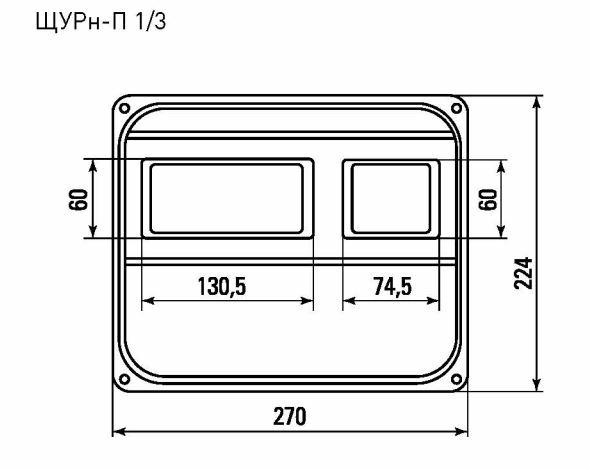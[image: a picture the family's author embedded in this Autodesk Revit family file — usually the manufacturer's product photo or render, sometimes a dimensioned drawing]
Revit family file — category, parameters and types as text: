
# Revit family: EKF_EE_ЩУРв_IP31_PROxima
name_source: partatom
category: Электрооборудование
units: mm (PartAtom-declared; Revit-internal decimal feet)

## family parameters
Всегда вертикально = Да
На основе рабочей плоскости = Нет
Общий = Нет
При загрузке вырезать с полостями = Нет
Размер круглого соединителя = Использовать диаметр
Тип детали = Силовой щит
Точка расчета площади = Да

## types (7) — shared parameters
ADSK_Единица измерения = компл.
ADSK_Завод-изготовитель = EKF
ADSK_Классификация нагрузок = Прочее
ADSK_Количество = 1
ADSK_Коэффициент мощности = 1
ADSK_Напряжение = 400 В
ADSK_Номинальная мощность = 0 Вт
ADSK_Полная мощность = 0 В·А
ADSK_Ток = 125 А
Изготовитель = EKF
Серия номенклатуры = PROxima
Степень защиты IP = IP31
ТВ = EKF
Тип установки = Встраиваемый
zero-valued in all types: ADSK_Масса, Количество DIN-реек

## per-type parameters (varying)
| type | ADSK_Код изделия | ADSK_Количество фаз | ADSK_Марка | ADSK_Материал | ADSK_Наименование | ADSK_Обозначение | ADSK_Размер_Высота | ADSK_Размер_Глубина | ADSK_Размер_Ширина | Количество модулей на DIN-рейке | Максимальное количество модулей | Тип |
| ЩУРв 1/12 (440х340х140) IP31 EKF PROxima | mb13-1/12 | 1 | ЩУРв 1/12 IP31 | Белый_ABS-пластик | Щит учетно-распред. встраиваемый ЩУРв 1/12 (440х340х140) IP31 EKF PROxima | ЩУРв 1/12 IP31 | 440 мм | 140 мм | 340 мм | 12 | 12 | 9 мм |
| ЩУРв 3/9 (540x340x160) IP31 EKF PROxima | mb-13-3/9 | 3 | ЩУРв 3/9 IP31 | Белый_ABS-пластик | Щит учетно-распред. встраиваемый ЩУРв 3/9 (540x340x160) IP31 EKF PROxima | ЩУРв 3/9 IP31 | 540 мм | 160 мм | 340 мм | 9 | 9 | 10 мм |
| ЩУРв 3/12 (540х340х160) IP31 EKF PROxima | mb13-3/12 | 3 | ЩУРв 3/12 IP31 | Белый_ABS-пластик | Щит учетно-распред. встраиваемый ЩУРв 3/12 (540х340х160) IP31 EKF PROxima | ЩУРв 3/12 IP31 | 540 мм | 160 мм | 340 мм | 12 | 12 | 11 мм |
| ЩУРв 3/18 (540х440х160) IP31 EKF PROxima | mb13-3/18 | 3 | ЩУРв 3/18 IP31 | Белый_ABS-пластик | Щит учетно-распред. встраиваемый ЩУРв 3/18 (540х440х160) IP31 EKF PROxima | ЩУРв 3/18 IP31 | 540 мм | 160 мм | 440 мм | 18 | 18 | 12 мм |
| ЩУРв 3/24 (540х440х160) IP31 EKF PROxima | mb13-3/24 | 3 | ЩУРв 3/24 IP31 | Белый_ABS-пластик | Щит учетно-распред. встраиваемый ЩУРв 3/24 (540х440х160) IP31 EKF PROxima | ЩУРв 3/24 IP31 | 540 мм | 160 мм | 440 мм | 24 | 24 | 13 мм |
| ЩУРв 3/30 двухдверный (620х530х165) IP31 EKF PROxima | mb13-3/30-2 | 3 | ЩУРв 3/30 двухдверный IP31 | Белый_ABS-пластик | Щит учетно-распред. встраиваемый ЩУРв 3/30 двухдверный (620х530х165) IP31 EKF PROxima | ЩУРв 3/30 двухдверный IP31 | 620 мм | 165 мм | 660 мм | 30 | 30 | 14 мм |
| ЩУРв 3/48 двухдверный (620х660х165) IP31 EKF PROxima | mb13-3/48-2 | 3 | ЩУРв 3/48 двухдверный IP31 | RAL 7035_Сталь | Щит учетно-распред. встраиваемый ЩУРв 3/48 двухдверный (620х660х165) IP31 EKF PROxima | ЩУРв 3/48 двухдверный IP31 | 620 мм | 165 мм | 660 мм | 48 | 48 | 15 мм |
